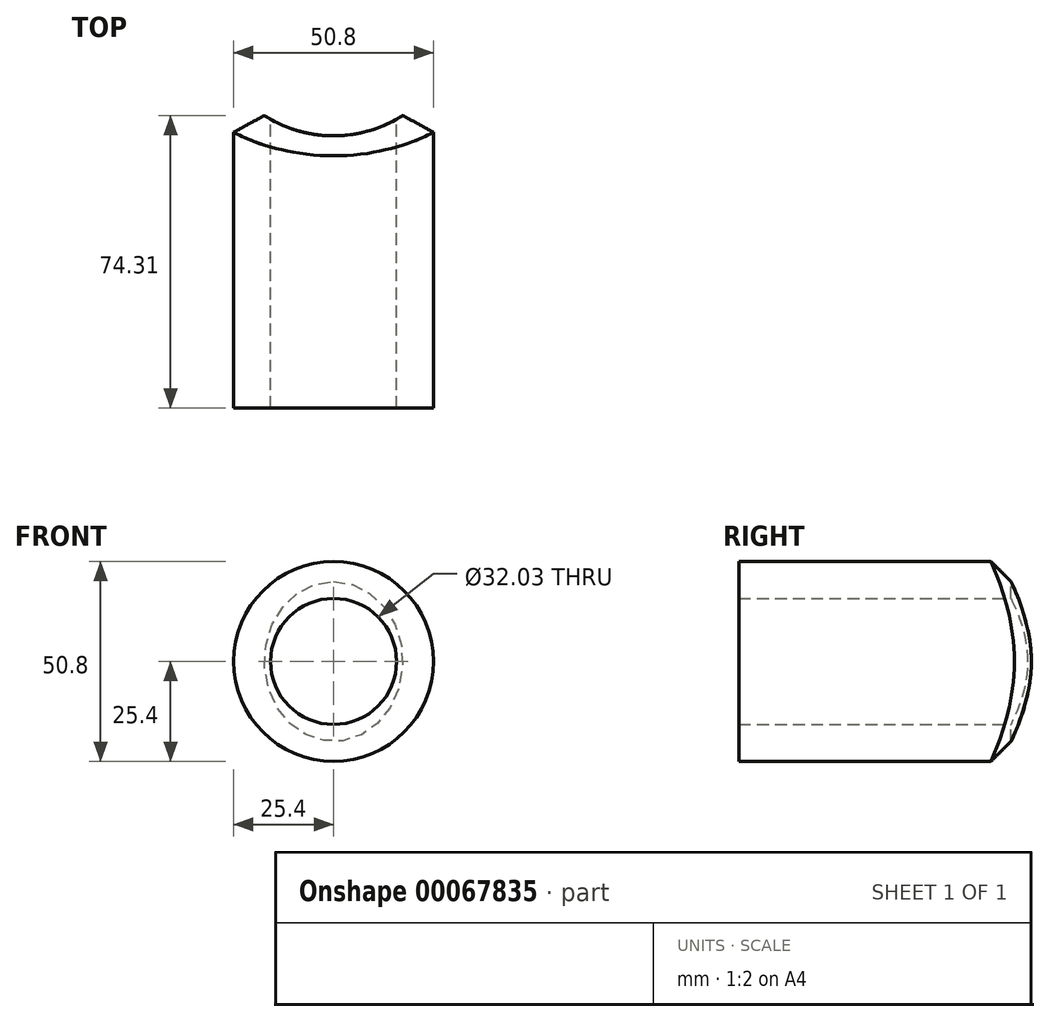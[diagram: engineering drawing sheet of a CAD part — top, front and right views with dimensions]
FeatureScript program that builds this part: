
annotation { "Feature Type Name" : "Feature", "Feature Type Description" : "" }
export const myFeature = defineFeature(function(context is Context, id is Id, definition is map)
    precondition{}
    {
        {
            var Q0;
            Q0=qCreatedBy(makeId("Front.planeOp"),FACE);
            var sketch = newSketch(context, id + "F0", { "sketchPlane" : qUnion([Q0])});
            skCircle(sketch, "E0", {"center": v(0, 0) * mm, "radius": 25.4 * mm});
            skSolve(sketch);
        }
        {
            var Q0;
            Q0=makeQuery(id+"F0.imprint","IMPRINT",FACE,{"disambiguationData":[TD([[makeQuery(id+"F0.imprint","IMPRINT",EDGE,{"derivedFrom":sQuery(id+"F0.wireOp",EDGE,"E0")}),1.0]])]});
            extrude(context, id + "F1", {"entities" : qUnion([Q0]), "depth" : 101.6 * mm});
        }
        {
            var Q0;
            Q0=qCreatedBy(makeId("Top.planeOp"),FACE);
            var sketch = newSketch(context, id + "F2", { "sketchPlane" : qUnion([Q0])});
            skCircle(sketch, "E1", {"center": v(0, 0) * mm, "radius": 32.46 * mm});
            skSolve(sketch);
        }
        {
            var Q0;
            Q0=makeQuery(id+"F2.imprint","IMPRINT",FACE,{"disambiguationData":[TD([[makeQuery(id+"F2.imprint","IMPRINT",EDGE,{"derivedFrom":sQuery(id+"F2.wireOp",EDGE,"E1")}),1.0]])]});
            extrude(context, id + "F3", {"entities" : qUnion([Q0]), "operationType" : NewBodyOperationType.REMOVE, "endBound" : BoundingType.THROUGH_ALL, "oppositeDirection" : true, "depth" : 25.4 * mm, "hasSecondDirection" : true, "secondDirectionOppositeDirection" : false, "secondDirectionDepth" : 25.4 * mm});
        }
        {
            var Q0;
            Q0=makeQuery(id+"F3.boolean.opBoolean","INTERSECT",EDGE,{"derivedFrom":[makeQuery(id+"F1.opExtrude","SWEPT_FACE",FACE,{"disambiguationData":[OSD([sQuery(id+"F0.wireOp",EDGE,"E0")])]}),makeQuery(id+"F3.opExtrude","SWEPT_FACE",FACE,{"disambiguationData":[OSD([sQuery(id+"F2.wireOp",EDGE,"E1")])]})]});
            chamfer(context, id + "F4", {"entities" : qUnion([Q0]), "width" : 5.08 * mm, "tangentPropagation" : true});
        }
        {
            var Q0;
            Q0=qCreatedBy(makeId("Front.planeOp"),FACE);
            var sketch = newSketch(context, id + "F5", { "sketchPlane" : qUnion([Q0])});
            skCircle(sketch, "E2", {"center": v(0, 0) * mm, "radius": 16.01 * mm});
            skSolve(sketch);
        }
        {
            var Q0;
            Q0=makeQuery(id+"F5.imprint","IMPRINT",FACE,{"disambiguationData":[TD([[makeQuery(id+"F5.imprint","IMPRINT",EDGE,{"derivedFrom":sQuery(id+"F5.wireOp",EDGE,"E2")}),1.0]])]});
            extrude(context, id + "F6", {"entities" : qUnion([Q0]), "operationType" : NewBodyOperationType.REMOVE, "endBound" : BoundingType.THROUGH_ALL, "depth" : 25.4 * mm});
        }
    });
